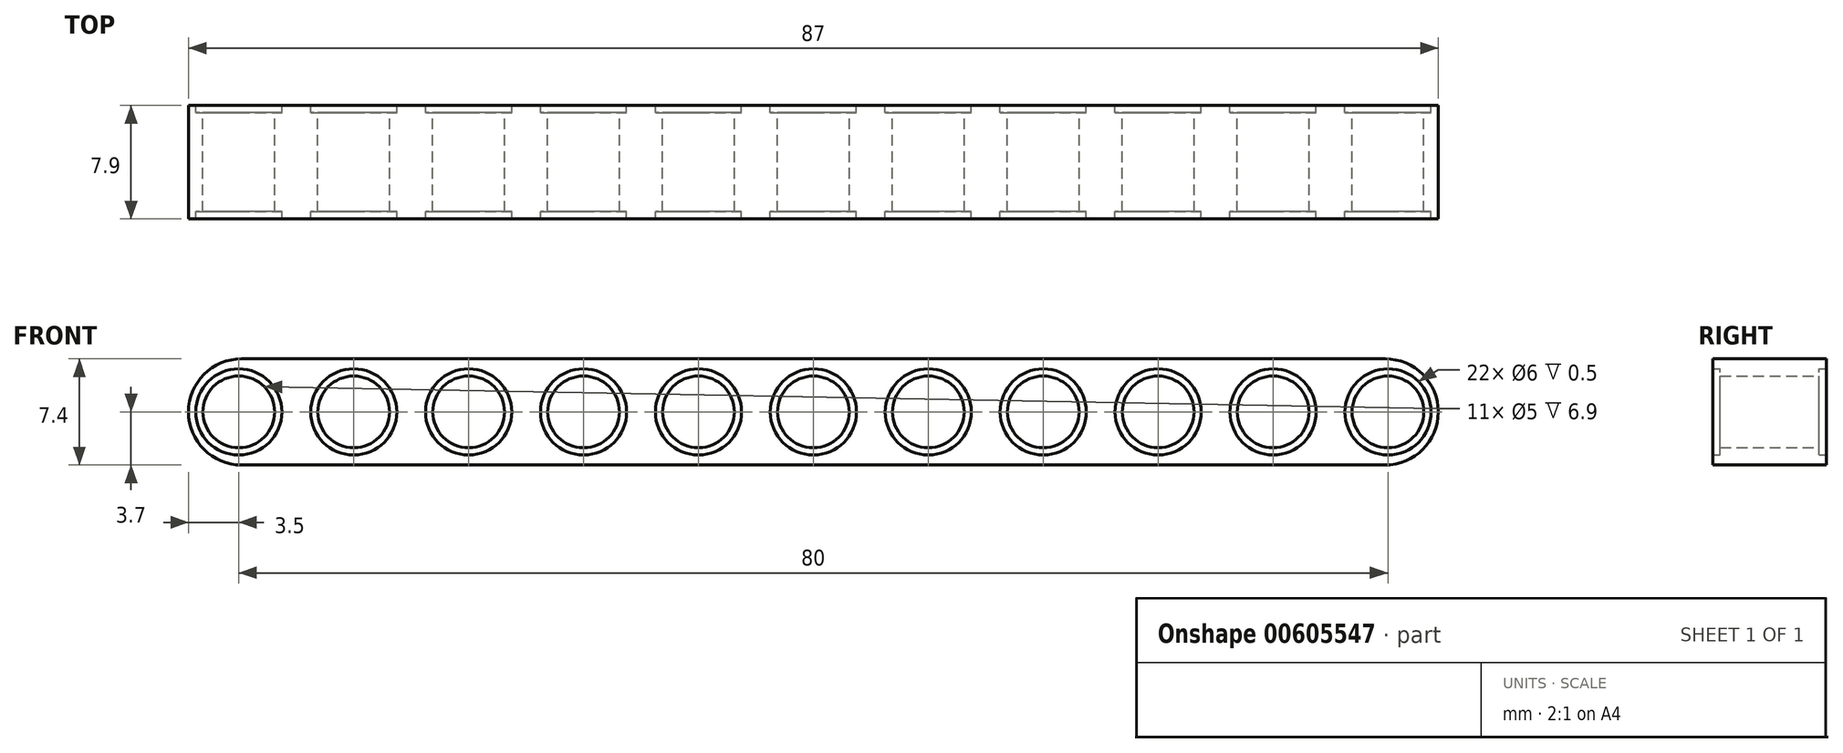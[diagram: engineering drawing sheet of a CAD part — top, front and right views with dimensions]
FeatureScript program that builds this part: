
annotation { "Feature Type Name" : "Feature", "Feature Type Description" : "" }
export const myFeature = defineFeature(function(context is Context, id is Id, definition is map)
    precondition{}
    {
        {
            var Q0;
            Q0=qCreatedBy(makeId("Front.planeOp"),FACE);
            var sketch = newSketch(context, id + "F0", { "sketchPlane" : qUnion([Q0])});
            skLineSegment(sketch, "E0", {"start": v(0, 0) * mm, "end": v(43.5, 0) * mm});
            skLineSegment(sketch, "E1", {"start": v(43.5, 0) * mm, "end": v(-43.5, 0) * mm});
            skLineSegment(sketch, "E2", {"start": v(-43.5, 0) * mm, "end": v(-43.5, 7.4) * mm});
            skLineSegment(sketch, "E3", {"start": v(-43.5, 7.4) * mm, "end": v(43.5, 7.4) * mm});
            skLineSegment(sketch, "E4", {"start": v(43.5, 7.4) * mm, "end": v(43.5, 0) * mm});
            skLineSegment(sketch, "E5", {"start": v(0, 0) * mm, "end": v(0, 3.7) * mm, "construction": true});
            skPoint(sketch, "E5.endSnap0", {"position": v(43.5, 3.7) * mm});
            skCircle(sketch, "E6", {"center": v(0, 3.7) * mm, "radius": 3 * mm});
            skLineSegment(sketch, "E7", {"start": v(0, 3.7) * mm, "end": v(8, 3.7) * mm, "construction": true});
            skLineSegment(sketch, "E8", {"start": v(8, 3.7) * mm, "end": v(16, 3.7) * mm, "construction": true});
            skLineSegment(sketch, "E9", {"start": v(16, 3.7) * mm, "end": v(24, 3.7) * mm, "construction": true});
            skLineSegment(sketch, "E10", {"start": v(24, 3.7) * mm, "end": v(32, 3.7) * mm, "construction": true});
            skLineSegment(sketch, "E11", {"start": v(32, 3.7) * mm, "end": v(40, 3.7) * mm, "construction": true});
            skLineSegment(sketch, "E12", {"start": v(0, 3.7) * mm, "end": v(-8, 3.7) * mm, "construction": true});
            skLineSegment(sketch, "E13", {"start": v(-8, 3.7) * mm, "end": v(-16, 3.7) * mm, "construction": true});
            skLineSegment(sketch, "E14", {"start": v(-16, 3.7) * mm, "end": v(-24, 3.7) * mm, "construction": true});
            skLineSegment(sketch, "E15", {"start": v(-24, 3.7) * mm, "end": v(-32, 3.7) * mm, "construction": true});
            skLineSegment(sketch, "E16", {"start": v(-32, 3.7) * mm, "end": v(-40, 3.7) * mm, "construction": true});
            skCircle(sketch, "E17", {"center": v(-40, 3.7) * mm, "radius": 3 * mm});
            skCircle(sketch, "E18", {"center": v(-32, 3.7) * mm, "radius": 3 * mm});
            skCircle(sketch, "E19", {"center": v(-16, 3.7) * mm, "radius": 3 * mm});
            skCircle(sketch, "E20", {"center": v(-8, 3.7) * mm, "radius": 3 * mm});
            skCircle(sketch, "E21", {"center": v(8, 3.7) * mm, "radius": 3 * mm});
            skCircle(sketch, "E22", {"center": v(16, 3.7) * mm, "radius": 3 * mm});
            skCircle(sketch, "E23", {"center": v(24, 3.7) * mm, "radius": 3 * mm});
            skCircle(sketch, "E24", {"center": v(32, 3.7) * mm, "radius": 3 * mm});
            skCircle(sketch, "E25", {"center": v(40, 3.7) * mm, "radius": 3 * mm});
            skCircle(sketch, "E26", {"center": v(-40, 3.7) * mm, "radius": 2.5 * mm});
            skCircle(sketch, "E27", {"center": v(-32, 3.7) * mm, "radius": 2.5 * mm});
            skCircle(sketch, "E28", {"center": v(-16, 3.7) * mm, "radius": 2.5 * mm});
            skCircle(sketch, "E29", {"center": v(0, 3.7) * mm, "radius": 2.5 * mm});
            skCircle(sketch, "E30", {"center": v(8, 3.7) * mm, "radius": 2.5 * mm});
            skCircle(sketch, "E31", {"center": v(16, 3.7) * mm, "radius": 2.5 * mm});
            skCircle(sketch, "E32", {"center": v(24, 3.7) * mm, "radius": 2.5 * mm});
            skCircle(sketch, "E33", {"center": v(32, 3.7) * mm, "radius": 2.5 * mm});
            skCircle(sketch, "E34", {"center": v(40, 3.7) * mm, "radius": 2.5 * mm});
            skCircle(sketch, "E35", {"center": v(-24, 3.7) * mm, "radius": 3 * mm});
            skCircle(sketch, "E36", {"center": v(-24, 3.7) * mm, "radius": 2.5 * mm});
            skCircle(sketch, "E37", {"center": v(-8, 3.7) * mm, "radius": 2.5 * mm});
            skSolve(sketch);
        }
        {
            var Q0;
            {var subQ2=sQuery(id+"F0.wireOp",EDGE,"E2");Q0=makeQuery(id+"F0.imprint","IMPRINT",FACE,{"disambiguationData":[TD([[makeQuery(id+"F0.imprint","IMPRINT",EDGE,{"derivedFrom":subQ2}),-1.0]])]});}
            extrude(context, id + "F1", {"entities" : qUnion([Q0]), "endBound" : BoundingType.SYMMETRIC, "depth" : 7.9 * mm, "offsetDistance" : 25 * mm});
        }
        {
            var Q0;
            Q0=makeQuery(id+"F0.imprint","IMPRINT",FACE,{"disambiguationData":[TD([[makeQuery(id+"F0.imprint","IMPRINT",EDGE,{"derivedFrom":sQuery(id+"F0.wireOp",EDGE,"E17")}),1.0]])]});
            var Q1;
            Q1=makeQuery(id+"F0.imprint","IMPRINT",FACE,{"disambiguationData":[TD([[makeQuery(id+"F0.imprint","IMPRINT",EDGE,{"derivedFrom":sQuery(id+"F0.wireOp",EDGE,"E18")}),1.0]])]});
            var Q2;
            Q2=makeQuery(id+"F0.imprint","IMPRINT",FACE,{"disambiguationData":[TD([[makeQuery(id+"F0.imprint","IMPRINT",EDGE,{"derivedFrom":sQuery(id+"F0.wireOp",EDGE,"E35")}),1.0]])]});
            var Q3;
            Q3=makeQuery(id+"F0.imprint","IMPRINT",FACE,{"disambiguationData":[TD([[makeQuery(id+"F0.imprint","IMPRINT",EDGE,{"derivedFrom":sQuery(id+"F0.wireOp",EDGE,"E19")}),1.0]])]});
            var Q4;
            Q4=makeQuery(id+"F0.imprint","IMPRINT",FACE,{"disambiguationData":[TD([[makeQuery(id+"F0.imprint","IMPRINT",EDGE,{"derivedFrom":sQuery(id+"F0.wireOp",EDGE,"E20")}),1.0]])]});
            var Q5;
            Q5=makeQuery(id+"F0.imprint","IMPRINT",FACE,{"disambiguationData":[TD([[makeQuery(id+"F0.imprint","IMPRINT",EDGE,{"derivedFrom":sQuery(id+"F0.wireOp",EDGE,"E6")}),1.0]])]});
            var Q6;
            Q6=makeQuery(id+"F0.imprint","IMPRINT",FACE,{"disambiguationData":[TD([[makeQuery(id+"F0.imprint","IMPRINT",EDGE,{"derivedFrom":sQuery(id+"F0.wireOp",EDGE,"E21")}),1.0]])]});
            var Q7;
            Q7=makeQuery(id+"F0.imprint","IMPRINT",FACE,{"disambiguationData":[TD([[makeQuery(id+"F0.imprint","IMPRINT",EDGE,{"derivedFrom":sQuery(id+"F0.wireOp",EDGE,"E22")}),1.0]])]});
            var Q8;
            Q8=makeQuery(id+"F0.imprint","IMPRINT",FACE,{"disambiguationData":[TD([[makeQuery(id+"F0.imprint","IMPRINT",EDGE,{"derivedFrom":sQuery(id+"F0.wireOp",EDGE,"E23")}),1.0]])]});
            var Q9;
            Q9=makeQuery(id+"F0.imprint","IMPRINT",FACE,{"disambiguationData":[TD([[makeQuery(id+"F0.imprint","IMPRINT",EDGE,{"derivedFrom":sQuery(id+"F0.wireOp",EDGE,"E24")}),1.0]])]});
            var Q10;
            Q10=makeQuery(id+"F0.imprint","IMPRINT",FACE,{"disambiguationData":[TD([[makeQuery(id+"F0.imprint","IMPRINT",EDGE,{"derivedFrom":sQuery(id+"F0.wireOp",EDGE,"E25")}),1.0]])]});
            extrude(context, id + "F2", {"entities" : qUnion([Q0, Q1, Q2, Q3, Q4, Q5, Q6, Q7, Q8, Q9, Q10]), "operationType" : NewBodyOperationType.ADD, "endBound" : BoundingType.SYMMETRIC, "depth" : 6.9 * mm, "offsetDistance" : 25 * mm});
        }
        {
            var Q0;
            Q0=makeQuery(id+"F1.opExtrude","SWEPT_EDGE",EDGE,{"disambiguationData":[OSD([sQuery(id+"F0.wireOp",EDGE,"E2"),sQuery(id+"F0.wireOp",EDGE,"E3")])]});
            var Q1;
            Q1=makeQuery(id+"F1.opExtrude","SWEPT_EDGE",EDGE,{"disambiguationData":[OSD([sQuery(id+"F0.wireOp",EDGE,"E1"),sQuery(id+"F0.wireOp",EDGE,"E2")])]});
            fillet(context, id + "F3", {"entities" : qUnion([Q0, Q1]), "radius" : 3.7 * mm, "tangentPropagation" : true, "allowEdgeOverflow" : false});
        }
        {
            var Q0;
            Q0=makeQuery(id+"F1.opExtrude","SWEPT_EDGE",EDGE,{"disambiguationData":[OSD([sQuery(id+"F0.wireOp",EDGE,"E3"),sQuery(id+"F0.wireOp",EDGE,"E4")])]});
            var Q1;
            Q1=makeQuery(id+"F1.opExtrude","SWEPT_EDGE",EDGE,{"disambiguationData":[OSD([sQuery(id+"F0.wireOp",EDGE,"E1"),sQuery(id+"F0.wireOp",EDGE,"E4")])]});
            fillet(context, id + "F4", {"entities" : qUnion([Q0, Q1]), "radius" : 3.7 * mm, "tangentPropagation" : true, "allowEdgeOverflow" : false});
        }
    });
